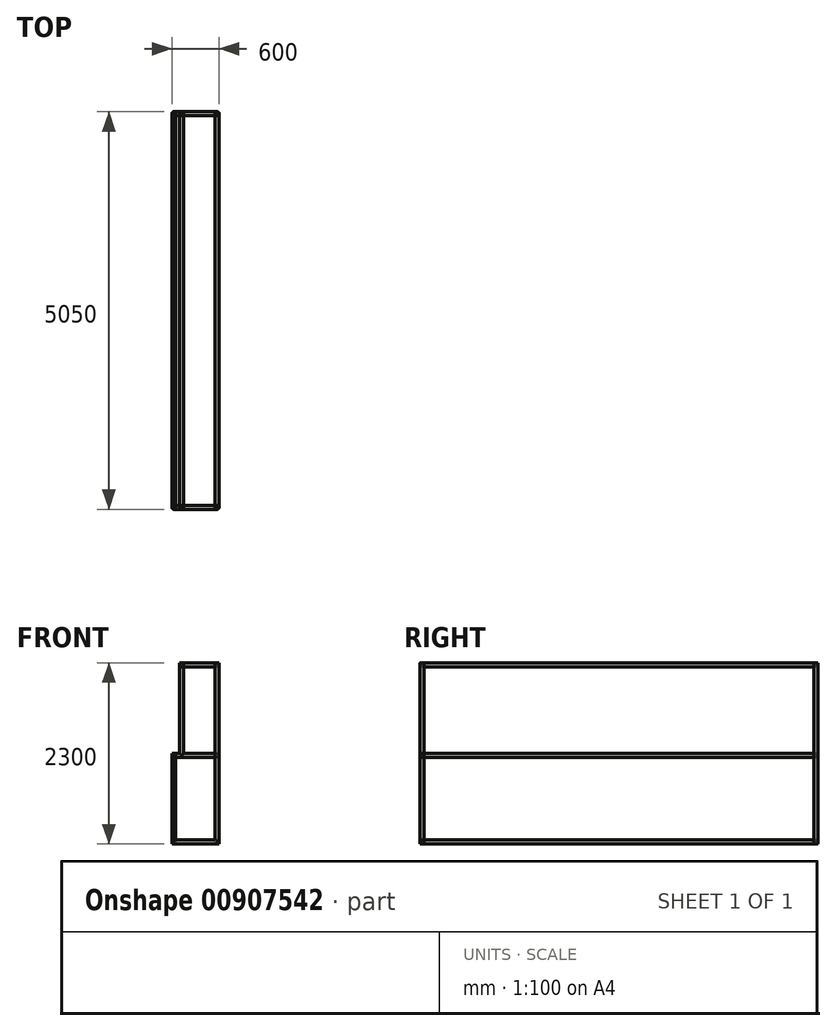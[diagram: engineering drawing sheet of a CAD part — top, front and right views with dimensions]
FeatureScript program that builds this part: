
annotation { "Feature Type Name" : "Feature", "Feature Type Description" : "" }
export const myFeature = defineFeature(function(context is Context, id is Id, definition is map)
    precondition{}
    {
        {
            var Q0;
            Q0=qCreatedBy(makeId("Right.planeOp"),FACE);
            var sketch = newSketch(context, id + "F0", { "sketchPlane" : qUnion([Q0])});
            skLineSegment(sketch, "E0.bottom", {"start": v(1500, -1152.5) * mm, "end": v(-1500, -1152.5) * mm});
            skLineSegment(sketch, "E0.top", {"start": v(1500, 1147.5) * mm, "end": v(-1500, 1147.5) * mm});
            skLineSegment(sketch, "E0.left", {"start": v(1500, -1152.5) * mm, "end": v(1500, 1147.5) * mm});
            skLineSegment(sketch, "E0.right", {"start": v(-1500, -1152.5) * mm, "end": v(-1500, 1147.5) * mm});
            skPoint(sketch, "E0.middle", {"position": v(0, -2.5) * mm});
            skPoint(sketch, "E1.middle", {"position": v(0, 0) * mm});
            skSolve(sketch);
        }
        {
            var Q0;
            Q0=qCreatedBy(makeId("Top.planeOp"),FACE);
            var sketch = newSketch(context, id + "F1", { "sketchPlane" : qUnion([Q0])});
            skLineSegment(sketch, "E2.bottom", {"start": v(300, -2500) * mm, "end": v(-300, -2500) * mm, "construction": true});
            skLineSegment(sketch, "E2.top", {"start": v(300, 2500) * mm, "end": v(-300, 2500) * mm, "construction": true});
            skLineSegment(sketch, "E2.left", {"start": v(300, -2500) * mm, "end": v(300, 2500) * mm, "construction": true});
            skLineSegment(sketch, "E2.right", {"start": v(-300, -2500) * mm, "end": v(-300, 2500) * mm, "construction": true});
            skPoint(sketch, "E2.middle", {"position": v(0, 0) * mm});
            skCircle(sketch, "E3", {"center": v(-275, 2500) * mm, "radius": 25 * mm, "construction": true});
            skCircle(sketch, "E4", {"center": v(275, 2500) * mm, "radius": 25 * mm});
            skCircle(sketch, "E5", {"center": v(275, -2500) * mm, "radius": 25 * mm});
            skCircle(sketch, "E6", {"center": v(-275, -2500) * mm, "radius": 25 * mm, "construction": true});
            skSolve(sketch);
        }
        {
            var Q0;
            Q0 = qSketchRegion(id + "F1", true);
            extrude(context, id + "F2", {"entities" : qUnion([Q0]), "depth" : 2300 * mm, "offsetDistance" : 25 * mm});
        }
        {
            var Q0;
            Q0=qCreatedBy(makeId("Top.planeOp"),FACE);
            var sketch = newSketch(context, id + "F3", { "sketchPlane" : qUnion([Q0])});
            skCircle(sketch, "E7", {"center": v(-275, -2500) * mm, "radius": 25 * mm});
            skCircle(sketch, "E8", {"center": v(-275, 2500) * mm, "radius": 25 * mm});
            skSolve(sketch);
        }
        {
            var Q0;
            Q0 = qSketchRegion(id + "F3", true);
            extrude(context, id + "F4", {"entities" : qUnion([Q0]), "depth" : 1150 * mm, "offsetDistance" : 25 * mm});
        }
        {
            var Q0;
            Q0=qCreatedBy(makeId("Front.planeOp"),FACE);
            var sketch = newSketch(context, id + "F5", { "sketchPlane" : qUnion([Q0])});
            skCircle(sketch, "E9", {"center": v(275, 2275) * mm, "radius": 25 * mm, "construction": true});
            skCircle(sketch, "E10", {"center": v(275, 25) * mm, "radius": 25 * mm});
            skCircle(sketch, "E11", {"center": v(275, 1125) * mm, "radius": 25 * mm});
            skCircle(sketch, "E12", {"center": v(-275, 1125) * mm, "radius": 25 * mm});
            skLineSegment(sketch, "E13", {"start": v(0, 2275) * mm, "end": v(0, 0) * mm, "construction": true});
            skLineSegment(sketch, "E14", {"start": v(-275, 2275) * mm, "end": v(275, 2275) * mm, "construction": true});
            skCircle(sketch, "E15", {"center": v(-275, 25) * mm, "radius": 25 * mm});
            skCircle(sketch, "E16", {"center": v(-175, 2275) * mm, "radius": 25 * mm});
            skSolve(sketch);
        }
        {
            var Q0;
            Q0 = qSketchRegion(id + "F5", true);
            extrude(context, id + "F6", {"entities" : qUnion([Q0]), "depth" : 2500 * mm, "offsetDistance" : 25 * mm, "hasSecondDirection" : true, "secondDirectionOppositeDirection" : true, "secondDirectionDepth" : 2500 * mm});
        }
        {
            var Q0;
            Q0=makeQuery(id+"F0.imprint","IMPRINT",FACE,{"disambiguationData":[TD([[makeQuery(id+"F0.imprint","IMPRINT",EDGE,{"derivedFrom":sQuery(id+"F0.wireOp",EDGE,"E0.bottom")}),-1.0]])]});
            var sketch = newSketch(context, id + "F7", { "sketchPlane" : qUnion([Q0])});
            skCircle(sketch, "E17", {"center": v(-2500, 2275) * mm, "radius": 25 * mm, "construction": true});
            skCircle(sketch, "E18", {"center": v(2500, 2275) * mm, "radius": 25 * mm, "construction": true});
            skCircle(sketch, "E19", {"center": v(2500, 25) * mm, "radius": 25 * mm});
            skCircle(sketch, "E20", {"center": v(-2500, 25) * mm, "radius": 25 * mm});
            skCircle(sketch, "E21", {"center": v(-2500, 1125) * mm, "radius": 25 * mm});
            skCircle(sketch, "E22", {"center": v(2500, 1125) * mm, "radius": 25 * mm});
            skSolve(sketch);
        }
        {
            var Q0;
            Q0 = qSketchRegion(id + "F7", true);
            extrude(context, id + "F8", {"entities" : qUnion([Q0]), "depth" : 280 * mm, "offsetDistance" : 25 * mm, "hasSecondDirection" : true, "secondDirectionOppositeDirection" : true, "secondDirectionDepth" : 280 * mm});
        }
        {
            var Q0;
            Q0=qCreatedBy(makeId("Top.planeOp"),FACE);
            cPlane(context, id + "F9", {"entities" : qUnion([Q0]), "cplaneType" : CPlaneType.OFFSET, "offset" : 1125 * mm, "width" : 150 * mm, "height" : 150 * mm});
        }
        {
            var Q0;
            Q0=qCreatedBy(id+"F9.planeOp",FACE);
            var sketch = newSketch(context, id + "F10", { "sketchPlane" : qUnion([Q0])});
            skCircle(sketch, "E23", {"center": v(-175, -2500) * mm, "radius": 25 * mm});
            skCircle(sketch, "E24", {"center": v(-175, 2500) * mm, "radius": 25 * mm});
            skSolve(sketch);
        }
        {
            var Q0;
            Q0 = qSketchRegion(id + "F10", true);
            var Q1;
            Q1=makeQuery(id+"F2.opExtrude","CAP_FACE",FACE,{"disambiguationData":[OSD([sQuery(id+"F1.wireOp",EDGE,"E5")])],"isStart":false});
            extrude(context, id + "F11", {"entities" : qUnion([Q0]), "operationType" : NewBodyOperationType.ADD, "endBound" : BoundingType.UP_TO_SURFACE, "depth" : 25 * mm, "endBoundEntityFace" : qUnion([Q1]), "offsetDistance" : 25 * mm});
        }
        {
            var Q0;
            Q0=qCreatedBy(makeId("Right.planeOp"),FACE);
            var sketch = newSketch(context, id + "F12", { "sketchPlane" : qUnion([Q0])});
            skCircle(sketch, "E25", {"center": v(-2500, 2275) * mm, "radius": 25 * mm});
            skCircle(sketch, "E26", {"center": v(2500, 2275) * mm, "radius": 25 * mm});
            skSolve(sketch);
        }
        {
            var Q0;
            Q0 = qSketchRegion(id + "F12", true);
            extrude(context, id + "F13", {"entities" : qUnion([Q0]), "depth" : 275 * mm, "offsetDistance" : 25 * mm, "hasSecondDirection" : true, "secondDirectionOppositeDirection" : true, "secondDirectionDepth" : 175 * mm});
        }
    });
